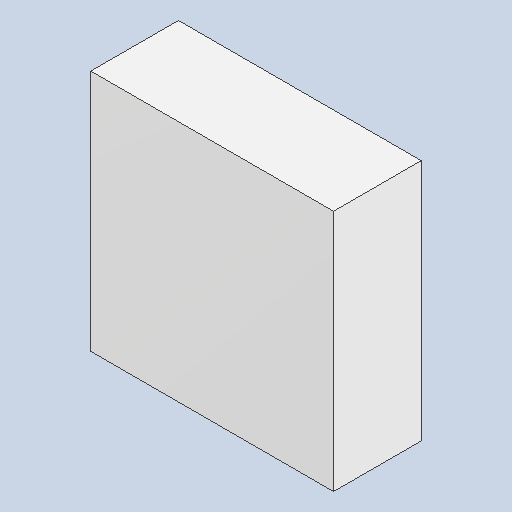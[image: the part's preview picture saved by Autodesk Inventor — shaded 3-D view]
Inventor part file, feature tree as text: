
AUTODESK INVENTOR PART (.ipt)
format: ipt  version: 2023.4 (Build 274418000, 418)  size: 81,408 bytes
history: native  units: mm
features: extrude x1
ambient origin geometry x8: Origin, YZ Plane, XZ Plane, XY Plane, X Axis, Y Axis, Z Axis, Center Point
bodies: Solid1 (feature_tree)
feature tree (1):
  extrude  "Extruded"  [1 undecoded]
note: 1 required parameter value undecoded (feature->parameter linkage not recoverable at this tier; creation-order binding heuristic only, values carry confidence <= 0.55)
